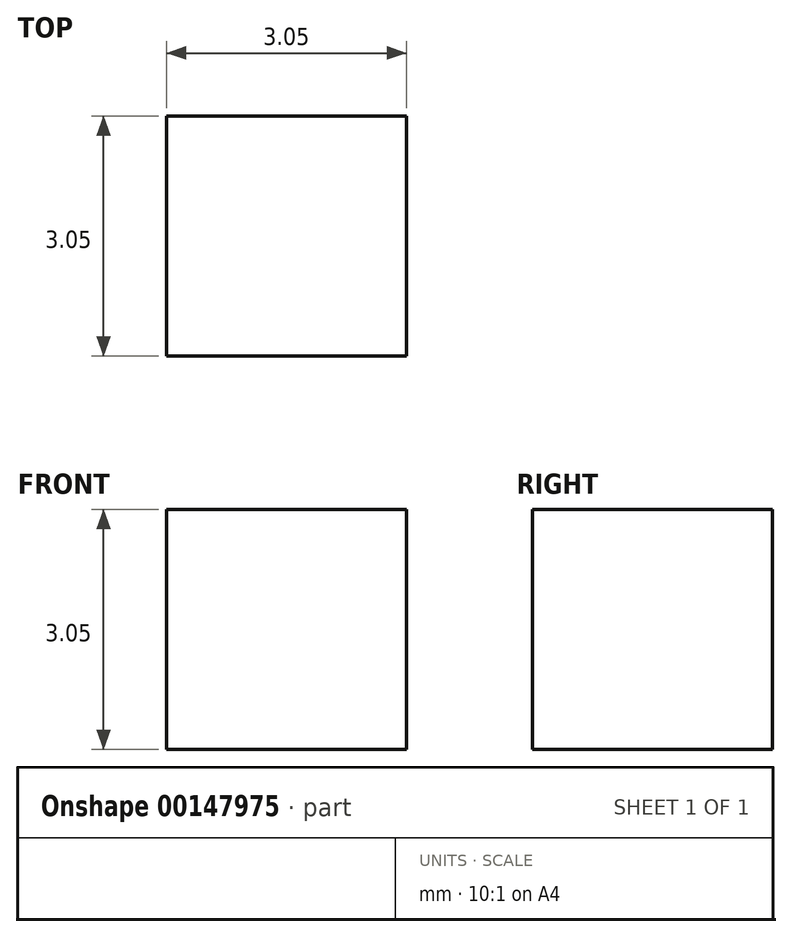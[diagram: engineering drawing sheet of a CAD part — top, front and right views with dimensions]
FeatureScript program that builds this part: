
annotation { "Feature Type Name" : "Feature", "Feature Type Description" : "" }
export const myFeature = defineFeature(function(context is Context, id is Id, definition is map)
    precondition{}
    {
        {
            var Q0;
            Q0=qCreatedBy(makeId("Top.planeOp"),FACE);
            var sketch = newSketch(context, id + "F0", { "sketchPlane" : qUnion([Q0])});
            skLineSegment(sketch, "E0.bottom", {"start": v(0, 0) * mm, "end": v(3.05, 0) * mm});
            skLineSegment(sketch, "E0.top", {"start": v(0, -3.05) * mm, "end": v(3.05, -3.05) * mm});
            skLineSegment(sketch, "E0.left", {"start": v(0, 0) * mm, "end": v(0, -3.05) * mm});
            skLineSegment(sketch, "E0.right", {"start": v(3.05, 0) * mm, "end": v(3.05, -3.05) * mm});
            skSolve(sketch);
        }
        {
            var Q0;
            Q0=qSketchRegion(id+"F0",true);
            extrude(context, id + "F1", {"entities" : qUnion([Q0]), "depth" : 3.05 * mm});
        }
    });
